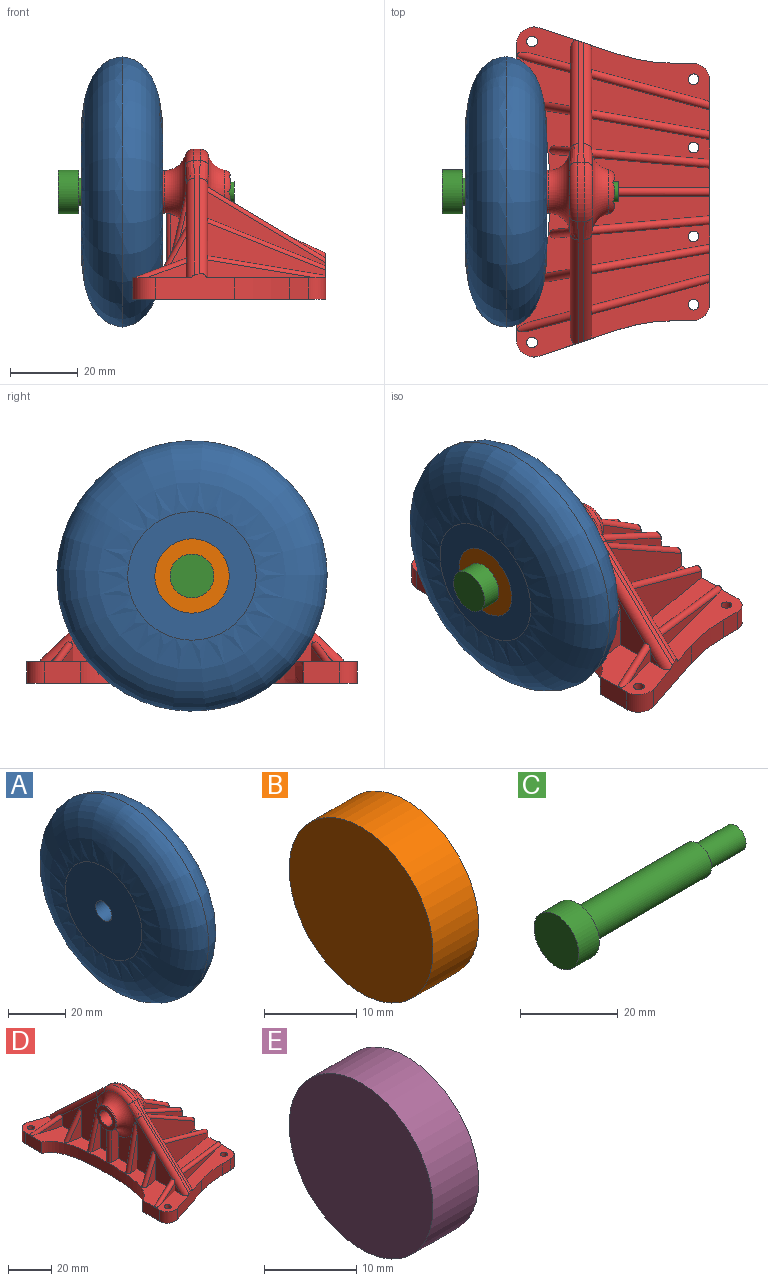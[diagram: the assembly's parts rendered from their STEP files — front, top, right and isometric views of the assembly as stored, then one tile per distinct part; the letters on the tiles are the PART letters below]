
ASSEMBLY  parts=5 mates=4
PART A: 5 faces, bbox 24x80x80 mm
  f0: cylinder r=4mm len=24mm, axis (-1,0,0), area 603.2mm2, adj f1,f4
  f1: plane 38x38mm, normal (1,0,0), area 1083.8mm2, adj f0,f2
  f2: revolved ~80x80mm, area 5252.7mm2, adj f1,f3
  f3: revolved ~80x80mm, area 5252.7mm2, adj f2,f4
  f4: plane 38x38mm, normal (-1,0,0), area 1083.8mm2, adj f0,f3
PART B: 3 faces, bbox 7x22x22 mm
  f0: plane 22x22mm, normal (1,0,0), area 380.1mm2, adj f1
  f1: cylinder r=11mm len=22mm, axis (-1,0,0), area 483.8mm2, adj f0,f2
  f2: plane 22x22mm, normal (-1,0,0), area 380.1mm2, adj f1
PART C: 7 faces, bbox 52x13x13 mm
  f0: cylinder r=6.5mm len=13mm, axis (1,0,0), area 245mm2, adj f1,f6
  f1: plane 13x13mm, normal (-1,0,0), area 132.7mm2, adj f0
  f2: plane 6x6mm, normal (1,0,0), area 28.3mm2, adj f3
  f3: cylinder r=3mm len=11mm, axis (1,0,0), area 207.3mm2, adj f2,f4
  f4: plane 8x8mm, normal (1,0,0), area 22mm2, adj f3,f5
  f5: cylinder r=4mm len=35mm, axis (1,0,0), area 879.6mm2, adj f4,f6
  f6: plane 13x13mm, normal (1,0,0), area 82.5mm2, adj f0,f5
PART D: 120 faces, bbox 59.4x99.2x51.9 mm
  f0: plane 35.02x19.43mm, normal (0,-1,0), area 470mm2, adj f16,f41,f43,f44,f48,f74
  f1: plane 35.02x19.43mm, normal (0,1,0), area 470mm2, adj f16,f29,f32,f43,f48,f74
  f2: plane 34.93x24.94mm, normal (-0.09,1,0), area 517.1mm2, adj f15,f41,f43,f44,f48
  f3: plane 34.94x25.43mm, normal (0.09,-1,0), area 523.8mm2, adj f15,f40,f43,f46,f48
  f4: plane 34.93x16.31mm, normal (0.17,-0.98,0), area 329.4mm2, adj f14,f38,f39,f48
  f5: plane 34.93x16.14mm, normal (-0.17,0.98,0), area 323.1mm2, adj f14,f40,f46,f48
  f6: plane 34.93x24.94mm, normal (-0.09,-1,0), area 517.1mm2, adj f12,f29,f32,f43,f48
  f7: plane 34.94x25.43mm, normal (0.09,1,0), area 523.8mm2, adj f12,f26,f27,f43,f48
  f8: plane 34.93x16.31mm, normal (0.17,0.98,0), area 329.4mm2, adj f11,f22,f24,f48
  f9: plane 34.93x16.14mm, normal (-0.17,-0.98,0), area 323.1mm2, adj f11,f26,f27,f48
  f10: cylinder r=1.27mm len=36.23mm, axis (-0.95,0.26,0.16), area 144mm2, adj f21,f22,f24,f28,f48,f52,f99,f100
  f11: cylinder r=1.27mm len=36.4mm, axis (-0.92,0.16,0.37), area 152.1mm2, adj f8,f9,f21,f22,f26,f48
  f12: cylinder r=1.27mm len=36.33mm, axis (-0.86,0.07,0.51), area 163.5mm2, adj f6,f7,f43,f48
  f13: cylinder r=1.27mm len=36.23mm, axis (0.95,0.26,-0.16), area 144mm2, adj f35,f36,f38,f39,f48,f61,f88,f89
  f14: cylinder r=1.27mm len=36.4mm, axis (0.92,0.16,-0.37), area 152.1mm2, adj f4,f5,f39,f46,f48,f61
  f15: cylinder r=1.27mm len=36.33mm, axis (0.86,0.07,-0.51), area 163.5mm2, adj f2,f3,f43,f48
  f16: cylinder r=1.27mm len=29.7mm, axis (0.91,0,-0.42), area 127.1mm2, adj f0,f1,f48,f74
  f17: plane 97.66x57.16mm, normal (0,0,-1), area 4244.1mm2, adj f19,f20,f45,f48,f49,f50,f51,f76
  f18: plane 99.1x18.66mm, normal (0,0,1), area 809.3mm2, adj f19,f20,f23,f25,f30,f31,f37,f42
  f19: plane 10.9x6.35mm, normal (-1,0,0), area 69.2mm2, adj f17,f18,f76,f101
  f20: plane 24.37x8.64mm, normal (0.32,0.95,0), area 162.3mm2, adj f17,f18,f21,f25,f52,f54,f102,f118
  f21: cylinder r=2.54mm len=31.92mm, axis (0,-0.73,0.69), area 163.5mm2, adj f10,f11,f20,f22,f26,f28,f52,f54
  f22: plane 16.55x10.68mm, normal (1,0,0), area 114.4mm2, adj f8,f10,f11,f21,f24,f99
  f23: plane 28.08x23.8mm, normal (-1,0,0), area 329.5mm2, adj f18,f25,f33,f94,f95,f96,f98,f103
  f24: plane 34.93x15.48mm, normal (0,0,1), area 269.9mm2, adj f8,f10,f22,f48,f99
  f25: cylinder r=2.54mm len=32.76mm, axis (0,0.73,-0.69), area 164.2mm2, adj f18,f20,f23,f30,f34,f54,f97,f103
  f26: plane 27.74x10.77mm, normal (1,0,0), area 210.2mm2, adj f7,f9,f11,f21,f27,f43
  f27: plane 34.93x12.06mm, normal (0,0,1), area 252.2mm2, adj f7,f9,f26,f48,f113
  f28: plane 5.61x5.28mm, normal (1,0,0), area 14.8mm2, adj f10,f21,f52,f100
  f29: plane 17.72x8.84mm, normal (1,0,0), area 127.6mm2, adj f1,f6,f32,f43
  f30: plane 3.91x3.68mm, normal (-1,0,0), area 7.2mm2, adj f18,f25,f97
  f31: plane 18.51x9.4mm, normal (-1,0,0), area 137.7mm2, adj f18,f33,f78,f93
  f32: plane 34.93x8.84mm, normal (0,0,1), area 255.5mm2, adj f1,f6,f29,f48
  f33: torus R=12.7mm, axis (1,0,0), area 451.6mm2, adj f23,f31,f34,f42,f47,f57,f62,f63
  f34: bspline ~7.84x7.6mm, area 26.8mm2, adj f25,f33,f54,f62,f90,f91,f92
  f35: plane 35.24x16.8mm, normal (0,0,1), area 262.4mm2, adj f13,f36,f45,f48,f51,f61,f89,f112
  f36: plane 5.61x5.28mm, normal (1,0,0), area 14.8mm2, adj f13,f35,f61,f89
  f37: plane 3.91x3.68mm, normal (-1,0,0), area 7.2mm2, adj f18,f64,f86
  f38: plane 34.93x15.48mm, normal (0,0,1), area 269.9mm2, adj f4,f13,f39,f48,f88
  f39: plane 16.55x10.68mm, normal (1,0,0), area 114.4mm2, adj f4,f13,f14,f38,f61,f88
  f40: plane 34.93x12.06mm, normal (0,0,1), area 252.2mm2, adj f3,f5,f46,f48,f111
  f41: plane 17.72x8.84mm, normal (1,0,0), area 127.6mm2, adj f0,f2,f43,f44
  f42: plane 18.51x9.4mm, normal (-1,0,0), area 137.7mm2, adj f18,f33,f77,f82
  f43: torus R=12.7mm, axis (-1,0,0), area 379.8mm2, adj f0,f1,f2,f3,f6,f7,f12,f15
  f44: plane 34.93x8.84mm, normal (0,0,1), area 255.5mm2, adj f0,f2,f41,f48
  f45: plane 24.37x8.64mm, normal (0.32,-0.95,0), area 162.3mm2, adj f17,f18,f35,f53,f61,f64,f101,f119
  f46: plane 27.74x10.77mm, normal (1,0,0), area 210.2mm2, adj f3,f5,f14,f40,f43,f61
  f47: plane 28.08x23.8mm, normal (-1,0,0), area 329.5mm2, adj f18,f33,f64,f83,f84,f85,f87,f106
  f48: plane 67.56x15.18mm, normal (1,0,0), area 484.7mm2, adj f0,f1,f2,f3,f4,f5,f6,f7
  f49: plane 6.35x5.73mm, normal (0,1,0), area 36.4mm2, adj f17,f52,f116,f118
  f50: plane 10.9x6.35mm, normal (-1,0,0), area 69.2mm2, adj f17,f18,f76,f102
  f51: plane 6.35x5.73mm, normal (0,-1,0), area 36.4mm2, adj f17,f35,f117,f119
  f52: plane 35.24x16.8mm, normal (0,0,1), area 262.4mm2, adj f10,f20,f21,f28,f48,f49,f100,f110
  f53: plane 35.96x33.85mm, normal (0,-0.69,0.73), area 65.2mm2, adj f45,f55,f60,f61,f63,f64
  f54: plane 35.96x33.85mm, normal (0,0.69,0.73), area 65.2mm2, adj f20,f21,f25,f34,f55,f58
  f55: cylinder r=12.7mm len=17.41mm, axis (1,0,0), area 38.6mm2, adj f53,f54,f59,f62
  f56: plane 12.7x12.7mm, normal (-1,0,0), area 76.4mm2, adj f57,f65
  f57: cylinder r=6.35mm len=12.7mm, axis (-1,0,0), area 25.3mm2, adj f33,f56
  f58: bspline ~7.84x7.6mm, area 26.9mm2, adj f21,f43,f54,f59
  f59: torus R=10.16mm, axis (1,0,0), area 59.3mm2, adj f43,f55,f58,f60
  f60: bspline ~9.06x8.92mm, area 26.9mm2, adj f43,f53,f59,f61
  f61: cylinder r=2.54mm len=31.92mm, axis (0,-0.73,-0.69), area 163.5mm2, adj f13,f14,f35,f36,f39,f45,f46,f53
  f62: torus R=10.16mm, axis (-1,0,0), area 59.3mm2, adj f33,f34,f55,f63
  f63: bspline ~9.06x8.92mm, area 26.8mm2, adj f33,f53,f62,f64,f79,f80,f81
  f64: cylinder r=2.54mm len=32.76mm, axis (0,0.73,0.69), area 164.2mm2, adj f18,f37,f45,f47,f53,f63,f86,f106
  f65: cylinder r=4mm len=10.16mm, axis (1,0,0), area 255.3mm2, adj f56,f66
  f66: plane 8x8mm, normal (-1,0,0), area 22mm2, adj f65,f75
  f67: plane 5.8x5mm, normal (0,0.87,-0.5), area 32.6mm2, adj f68,f72,f73,f74
  f68: plane 5.8x5mm, normal (0,0.87,0.5), area 32.6mm2, adj f67,f69,f73,f74
  f69: plane 5.8x5.77mm, normal (0,0,1), area 32.6mm2, adj f68,f70,f73,f74
  f70: plane 6.33x5.53mm, normal (0,-0.87,0.5), area 32.6mm2, adj f69,f71,f73,f74
  f71: plane 5.8x5mm, normal (0,-0.87,-0.5), area 32.6mm2, adj f70,f72,f73,f74
  f72: plane 5.8x5.77mm, normal (0,0,-1), area 32.6mm2, adj f67,f71,f73,f74
  f73: plane 11.55x10mm, normal (1,0,0), area 58.3mm2, adj f67,f68,f69,f70,f71,f72,f75
  f74: torus R=4.02mm, axis (-1,0,0), area 74.7mm2, adj f0,f1,f16,f43,f67,f68,f69,f70
  f75: cylinder r=3mm len=6mm, axis (-1,0,0), area 78.4mm2, adj f66,f73
  f76: extruded ~65.71x9.96mm, area 456.5mm2, adj f17,f18,f19,f50
  f77: plane 19.02x4.67mm, normal (0,-1,0), area 78.9mm2, adj f18,f33,f42,f109
  f78: plane 19.02x4.67mm, normal (0,1,0), area 78.9mm2, adj f18,f31,f33,f109
  f79: plane 0.31x0.23mm, normal (0.09,-1,0), area 0mm2, adj f63,f80,f81
  f80: plane 0.26x0.18mm, normal (0.56,0.05,0.82), area 0mm2, adj f63,f79,f81
  f81: plane 0.31x0.27mm, normal (-0.97,-0.08,0.23), area 0mm2, adj f63,f79,f80
  f82: plane 20.34x4.9mm, normal (-0.09,1,0), area 49.6mm2, adj f18,f33,f42,f108
  f83: plane 19.57x4.6mm, normal (0.09,-1,0), area 45.2mm2, adj f18,f47,f108
  f84: plane 13x7.26mm, normal (-0.17,0.98,0), area 47.9mm2, adj f18,f47,f107
  f85: plane 12.21x6.82mm, normal (0.17,-0.98,0), area 42.3mm2, adj f18,f47,f107
  f86: plane 11.73x4.39mm, normal (0.26,-0.97,0), area 26.4mm2, adj f18,f37,f64,f106
  f87: plane 12.33x4.61mm, normal (-0.26,0.97,0), area 29.4mm2, adj f18,f47,f106
  f88: plane 31.09x8.33mm, normal (-0.26,0.97,0), area 83mm2, adj f13,f38,f39
  f89: plane 31.75x8.51mm, normal (0.26,-0.97,0), area 86.5mm2, adj f13,f35,f36
  f90: plane 0.31x0.23mm, normal (0.09,1,0), area 0mm2, adj f34,f91,f92
  f91: plane 0.26x0.18mm, normal (0.56,-0.05,0.82), area 0mm2, adj f34,f90,f92
  f92: plane 0.31x0.27mm, normal (-0.97,0.08,0.23), area 0mm2, adj f34,f90,f91
  f93: plane 20.34x4.9mm, normal (-0.09,-1,0), area 49.6mm2, adj f18,f31,f33,f105
  f94: plane 19.57x4.6mm, normal (0.09,1,0), area 45.2mm2, adj f18,f23,f105
  f95: plane 13x7.26mm, normal (-0.17,-0.98,0), area 47.9mm2, adj f18,f23,f104
  f96: plane 12.21x6.82mm, normal (0.17,0.98,0), area 42.3mm2, adj f18,f23,f104
  f97: plane 11.73x4.39mm, normal (0.26,0.97,0), area 26.4mm2, adj f18,f25,f30,f103
  f98: plane 12.33x4.61mm, normal (-0.26,-0.97,0), area 29.4mm2, adj f18,f23,f103
  f99: plane 31.09x8.33mm, normal (-0.26,-0.97,0), area 83mm2, adj f10,f22,f24
  f100: plane 31.75x8.51mm, normal (0.26,0.97,0), area 86.5mm2, adj f10,f28,f52
  f101: cylinder r=5.08mm len=6.69mm, axis (0,0,-1), area 61mm2, adj f17,f18,f19,f45
  f102: cylinder r=5.08mm len=6.69mm, axis (0,0,-1), area 61mm2, adj f17,f18,f20,f50
  f103: cylinder r=1.27mm len=16.6mm, axis (-0.91,0.24,-0.34), area 62.9mm2, adj f18,f23,f25,f97,f98
  f104: cylinder r=1.27mm len=15.22mm, axis (-0.49,0.09,-0.87), area 63.5mm2, adj f18,f23,f95,f96
  f105: cylinder r=1.27mm len=25.37mm, axis (-0.23,0.02,-0.97), area 93.4mm2, adj f18,f23,f33,f93,f94
  f106: cylinder r=1.27mm len=16.6mm, axis (0.91,0.24,0.34), area 62.9mm2, adj f18,f47,f64,f86,f87
  f107: cylinder r=1.27mm len=15.22mm, axis (0.49,0.09,0.87), area 63.5mm2, adj f18,f47,f84,f85
  f108: cylinder r=1.27mm len=25.37mm, axis (0.23,0.02,0.97), area 93.4mm2, adj f18,f33,f47,f82,f83
  f109: cylinder r=1.27mm len=19.03mm, axis (0,0,1), area 75.7mm2, adj f18,f33,f77,f78
  f110: cylinder r=1.59mm len=6.35mm, axis (0,0,-1), area 63.3mm2, adj f17,f52
  f111: cylinder r=1.59mm len=6.35mm, axis (0,0,-1), area 63.3mm2, adj f17,f40
  f112: cylinder r=1.59mm len=6.35mm, axis (0,0,-1), area 63.3mm2, adj f17,f35
  f113: cylinder r=1.59mm len=6.35mm, axis (0,0,-1), area 63.3mm2, adj f17,f27
  f114: cylinder r=1.59mm len=6.35mm, axis (0,0,-1), area 63.3mm2, adj f17,f18
  f115: cylinder r=1.59mm len=6.35mm, axis (0,0,-1), area 63.3mm2, adj f17,f18
  f116: cylinder r=5.08mm len=6.35mm, axis (0,0,1), area 50.7mm2, adj f17,f48,f49,f52
  f117: cylinder r=5.08mm len=6.35mm, axis (0,0,-1), area 50.7mm2, adj f17,f35,f48,f51
  f118: cylinder r=50.8mm len=16.06mm, axis (0,0,-1), area 103.8mm2, adj f17,f20,f49,f52
  f119: cylinder r=50.8mm len=16.06mm, axis (0,0,1), area 103.8mm2, adj f17,f35,f45,f51
PART E: 3 faces, bbox 7x22x22 mm
  f0: plane 22x22mm, normal (-1,0,0), area 380.1mm2, adj f2
  f1: plane 22x22mm, normal (1,0,0), area 380.1mm2, adj f2
  f2: cylinder r=11mm len=22mm, axis (-1,0,0), area 483.8mm2, adj f0,f1
PLACE A rot(axis=(-1,0,0),58.9deg) t=(-36.39,-16.3,32.66)mm
PLACE B rot(axis=(1,0,0),31.1deg) t=(-36.39,27.29,21.9)mm
PLACE C t=(-36.39,10.87,17.33)mm
PLACE D t=(-36.39,10.87,17.33)mm fixed
PLACE E t=(-36.39,10.87,17.33)mm
MATE revolute A.f0 <-> E.f2  axis (1,0,0) through (-46.55,10.87,49.08)mm
MATE revolute B.f1 <-> A.f0  axis (-1,0,0) through (-70.55,10.87,49.08)mm
MATE revolute E.f2 <-> D.f57  axis (1,0,0) through (-46.55,10.87,49.08)mm
MATE revolute D.f75 <-> C.f0  axis (-1,0,0) through (-36.39,10.87,49.08)mm
